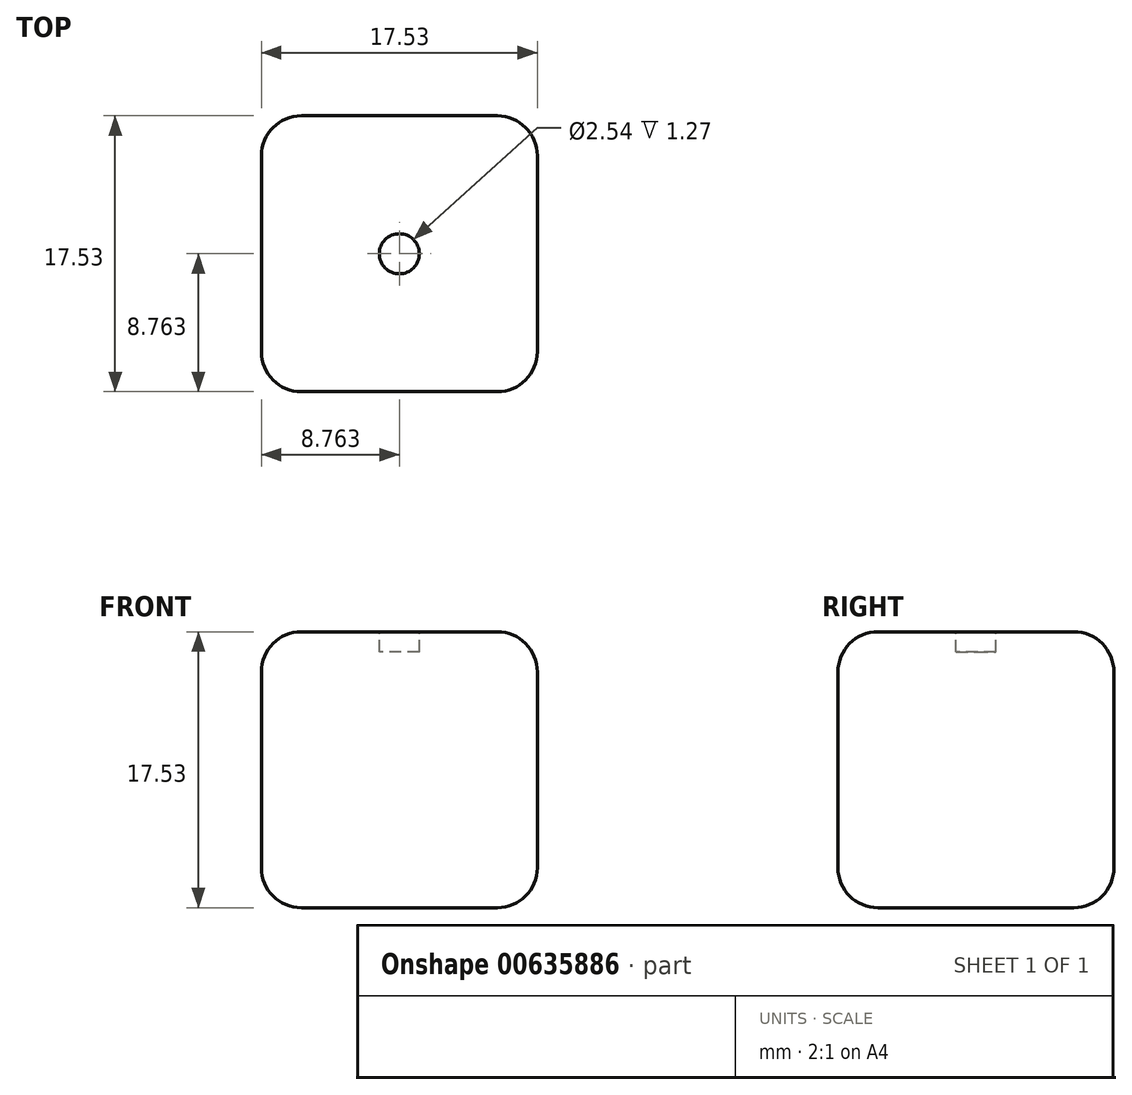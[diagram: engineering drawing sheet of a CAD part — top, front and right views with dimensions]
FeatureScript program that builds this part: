
annotation { "Feature Type Name" : "Feature", "Feature Type Description" : "" }
export const myFeature = defineFeature(function(context is Context, id is Id, definition is map)
    precondition{}
    {
        {
            var Q0;
            Q0=qCreatedBy(makeId("Top.planeOp"),FACE);
            var sketch = newSketch(context, id + "F0", { "sketchPlane" : qUnion([Q0])});
            skLineSegment(sketch, "E0.bottom", {"start": v(0, 0) * mm, "end": v(17.53, 0) * mm});
            skLineSegment(sketch, "E0.top", {"start": v(0, 17.53) * mm, "end": v(17.53, 17.53) * mm});
            skLineSegment(sketch, "E0.left", {"start": v(0, 0) * mm, "end": v(0, 17.53) * mm});
            skLineSegment(sketch, "E0.right", {"start": v(17.53, 0) * mm, "end": v(17.53, 17.53) * mm});
            skSolve(sketch);
        }
        {
            var Q0;
            Q0=makeQuery(id+"F0.imprint","IMPRINT",FACE,{"disambiguationData":[TD([[makeQuery(id+"F0.imprint","IMPRINT",EDGE,{"derivedFrom":sQuery(id+"F0.wireOp",EDGE,"E0.bottom")}),1.0]])]});
            extrude(context, id + "F1", {"entities" : qUnion([Q0]), "depth" : 17.53 * mm, "offsetDistance" : 25.4 * mm});
        }
        {
            var Q0;
            Q0=makeQuery(id+"F1.opExtrude","CAP_FACE",FACE,{"disambiguationData":[OSD([sQuery(id+"F0.wireOp",EDGE,"E0.bottom"),sQuery(id+"F0.wireOp",EDGE,"E0.top"),sQuery(id+"F0.wireOp",EDGE,"E0.left"),sQuery(id+"F0.wireOp",EDGE,"E0.right")])],"isStart":false});
            var Q1;
            Q1=makeQuery(id+"F1.opExtrude","SWEPT_FACE",FACE,{"disambiguationData":[OSD([sQuery(id+"F0.wireOp",EDGE,"E0.bottom")])]});
            var Q2;
            Q2=makeQuery(id+"F1.opExtrude","SWEPT_FACE",FACE,{"disambiguationData":[OSD([sQuery(id+"F0.wireOp",EDGE,"E0.right")])]});
            var Q3;
            Q3=makeQuery(id+"F1.opExtrude","SWEPT_FACE",FACE,{"disambiguationData":[OSD([sQuery(id+"F0.wireOp",EDGE,"E0.left")])]});
            var Q4;
            Q4=makeQuery(id+"F1.opExtrude","SWEPT_FACE",FACE,{"disambiguationData":[OSD([sQuery(id+"F0.wireOp",EDGE,"E0.top")])]});
            fillet(context, id + "F2", {"entities" : qUnion([Q0, Q1, Q2, Q3, Q4]), "radius" : 2.54 * mm, "tangentPropagation" : true, "allowEdgeOverflow" : false});
        }
        {
            var Q0;
            Q0=makeQuery(id+"F1.opExtrude","CAP_FACE",FACE,{"disambiguationData":[OSD([sQuery(id+"F0.wireOp",EDGE,"E0.bottom"),sQuery(id+"F0.wireOp",EDGE,"E0.top"),sQuery(id+"F0.wireOp",EDGE,"E0.left"),sQuery(id+"F0.wireOp",EDGE,"E0.right")])],"isStart":false});
            var sketch = newSketch(context, id + "F3", { "sketchPlane" : qUnion([Q0])});
            skCircle(sketch, "E1", {"center": v(8.76, 8.76) * mm, "radius": 1.27 * mm});
            skPoint(sketch, "E2.0", {"position": v(8.76, 14.99) * mm});
            skPoint(sketch, "E3.0", {"position": v(2.54, 8.76) * mm});
            skSolve(sketch);
        }
        {
            var Q0;
            Q0 = qSketchRegion(id + "F3", true);
            extrude(context, id + "F4", {"entities" : qUnion([Q0]), "operationType" : NewBodyOperationType.REMOVE, "oppositeDirection" : true, "depth" : 1.27 * mm, "offsetDistance" : 25.4 * mm});
        }
    });
